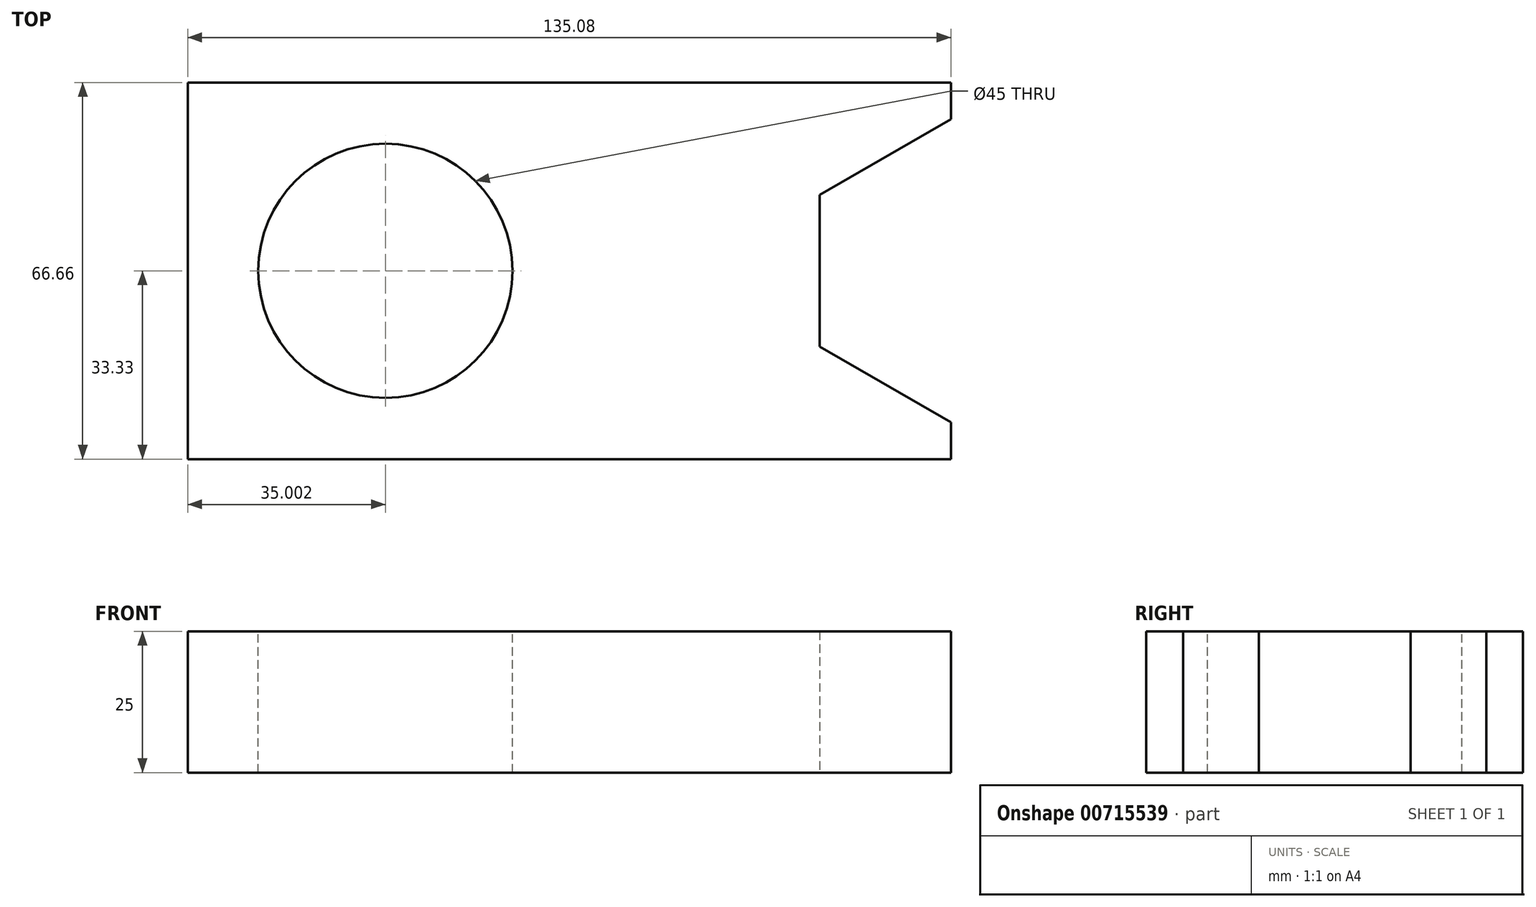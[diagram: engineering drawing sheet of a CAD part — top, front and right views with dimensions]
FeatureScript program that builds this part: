
annotation { "Feature Type Name" : "Feature", "Feature Type Description" : "" }
export const myFeature = defineFeature(function(context is Context, id is Id, definition is map)
    precondition{}
    {
        {
            var Q0;
            Q0=qCreatedBy(makeId("Top.planeOp"),FACE);
            var sketch = newSketch(context, id + "F0", { "sketchPlane" : qUnion([Q0])});
            skLineSegment(sketch, "E0.bottom", {"start": v(67.54, 33.33) * mm, "end": v(-67.54, 33.33) * mm});
            skLineSegment(sketch, "E0.top", {"start": v(67.54, -33.33) * mm, "end": v(-67.54, -33.33) * mm});
            skLineSegment(sketch, "E0.left", {"start": v(67.54, 33.33) * mm, "end": v(67.54, 26.84) * mm});
            skLineSegment(sketch, "E0.right", {"start": v(-67.54, 33.33) * mm, "end": v(-67.54, -33.33) * mm});
            skPoint(sketch, "E0.middle", {"position": v(0, 0) * mm});
            skArc(sketch, "E1.cCircle", {"start": v(79.16, 20.13) * mm, "mid": v(44.3, 0) * mm, "end": v(79.16, -20.13) * mm, "construction": true});
            skLineSegment(sketch, "E1.0", {"start": v(44.3, -13.42) * mm, "end": v(44.3, 13.42) * mm});
            skLineSegment(sketch, "E1.1", {"start": v(44.3, 13.42) * mm, "end": v(67.54, 26.84) * mm});
            skLineSegment(sketch, "E1.5", {"start": v(67.54, -26.84) * mm, "end": v(44.3, -13.42) * mm});
            skPoint(sketch, "E1.0.midPoint", {"position": v(44.3, 0) * mm});
            skLineSegment(sketch, "E2.trimOffspring", {"start": v(67.54, -26.84) * mm, "end": v(67.54, -33.33) * mm});
            skPoint(sketch, "E3.orphan", {"position": v(90.78, 13.42) * mm});
            skPoint(sketch, "E4.orphan", {"position": v(90.78, -13.42) * mm});
            skSolve(sketch);
        }
        {
            var Q0;
            Q0=makeQuery(id+"F0.imprint","IMPRINT",FACE,{"disambiguationData":[TD([[makeQuery(id+"F0.imprint","IMPRINT",EDGE,{"derivedFrom":sQuery(id+"F0.wireOp",EDGE,"E0.bottom")}),1.0]])]});
            extrude(context, id + "F1", {"entities" : qUnion([Q0]), "depth" : 25 * mm, "offsetDistance" : 25 * mm});
        }
        {
            var Q0;
            Q0=makeQuery(id+"F1.opExtrude","CAP_FACE",FACE,{"disambiguationData":[OSD([sQuery(id+"F0.wireOp",EDGE,"E0.bottom"),sQuery(id+"F0.wireOp",EDGE,"E0.top"),sQuery(id+"F0.wireOp",EDGE,"E0.left"),sQuery(id+"F0.wireOp",EDGE,"E0.right"),sQuery(id+"F0.wireOp",EDGE,"E1.0"),sQuery(id+"F0.wireOp",EDGE,"E1.1"),sQuery(id+"F0.wireOp",EDGE,"E1.5"),sQuery(id+"F0.wireOp",EDGE,"E2.trimOffspring")])],"isStart":false});
            var sketch = newSketch(context, id + "F2", { "sketchPlane" : qUnion([Q0])});
            skCircle(sketch, "E5", {"center": v(-32.54, 0) * mm, "radius": 22.5 * mm});
            skSolve(sketch);
        }
        {
            var Q0;
            Q0 = qSketchRegion(id + "F2", true);
            extrude(context, id + "F3", {"entities" : qUnion([Q0]), "operationType" : NewBodyOperationType.REMOVE, "oppositeDirection" : true, "depth" : 25 * mm, "offsetDistance" : 25 * mm});
        }
    });
